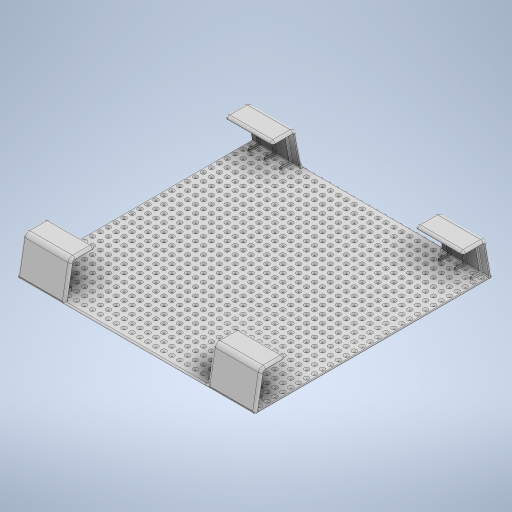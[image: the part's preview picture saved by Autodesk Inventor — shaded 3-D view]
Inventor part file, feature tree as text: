
AUTODESK INVENTOR PART (.ipt)
format: ipt  version: 2023 (Build 270158030, 158C)  size: 3,634,688 bytes
history: native  units: mm
features: fillet x10, extrude x5, sketch x4, plane x3, mirror x2, pattern_linear x1
ambient origin geometry x8: Origin, YZ Plane, XZ Plane, XY Plane, X Axis, Y Axis, Z Axis, Center Point
bodies: Solid1 (feature_tree)
feature tree (25):
  extrude  "Extrusion1"  Depth=150.0mm
  extrude  "Extrusion2"  Depth=3.0mm
  extrude  "Extrusion4"  Depth=120.0mm
  plane  "Work Plane1"
  extrude  "Extrusion5"  Depth=1.0mm TaperAngle=0.0deg
  fillet  "Fillet8"  Radius=1.0mm
  pattern_linear  "Rectangular Pattern1"  Spacing1=2.5mm  [1 undecoded]
  fillet  "Fillet13"  Radius=5.0mm
  fillet  "Fillet14"  Radius=300.0mm
  fillet  "Fillet15"  Radius=2.5mm
  plane  "Work Plane2"
  mirror  "Mirror1"
  plane  "Work Plane4"
  mirror  "Mirror3"
  fillet  "Fillet16"  Radius=5.0mm
  fillet  "Fillet17"  Radius=20.0mm
  fillet  "Fillet18"  Radius=2.0mm
  fillet  "Fillet19"  Radius=2.0mm
  extrude  "Extrusion3"  Depth=1.0mm
  fillet  "Fillet27"  Radius=15.0mm
  fillet  "Fillet28"  Radius=2.0mm
  sketch  "Sketch1"  dims[d0=150.0mm d1=150.0mm]
  sketch  "Sketch3"  dims[d2=1.5mm d3=0.0mm d4=3.0mm]
  sketch  "Sketch4"  dims[d5=90.0deg d6=120.0mm]
  sketch  "Sketch7"  dims[d7=90.0deg d8=3.0mm d9=0.0mm d10=1.0mm d11=2.5mm d12=5.0mm d13=300.0mm d15=5.0mm d16=300.0mm d18=5.0mm d21=2.5mm d23=5.0mm d24=0.0mm d29=20.0mm d30=2.0mm d31=2.0mm d32=13.962634mm d33=15.0mm d34=2.0mm d35=2.0mm d36=13.962634mm d37=15.0mm d41=30.0mm d42=30.0mm d43=10.0mm d44=10.0mm d45=1.5mm d46=0.0mm d48=6.0mm d49=1.3mm d50=1.3mm d51=1.3mm d52=7.0mm d53=-5.0mm d54=1.0mm d55=0.0mm d56=0.45mm d61=30.0mm d63=10.0mm d64=0.4mm d65=0.4mm d66=0.39mm d67=3.0mm d68=1.5mm d69=0.4mm d70=1.0mm d78=1.0mm d79=1.0mm d27=0.0mm d28=0.0mm]
note: 1 required parameter value undecoded (feature->parameter linkage not recoverable at this tier; creation-order binding heuristic only, values carry confidence <= 0.55)
